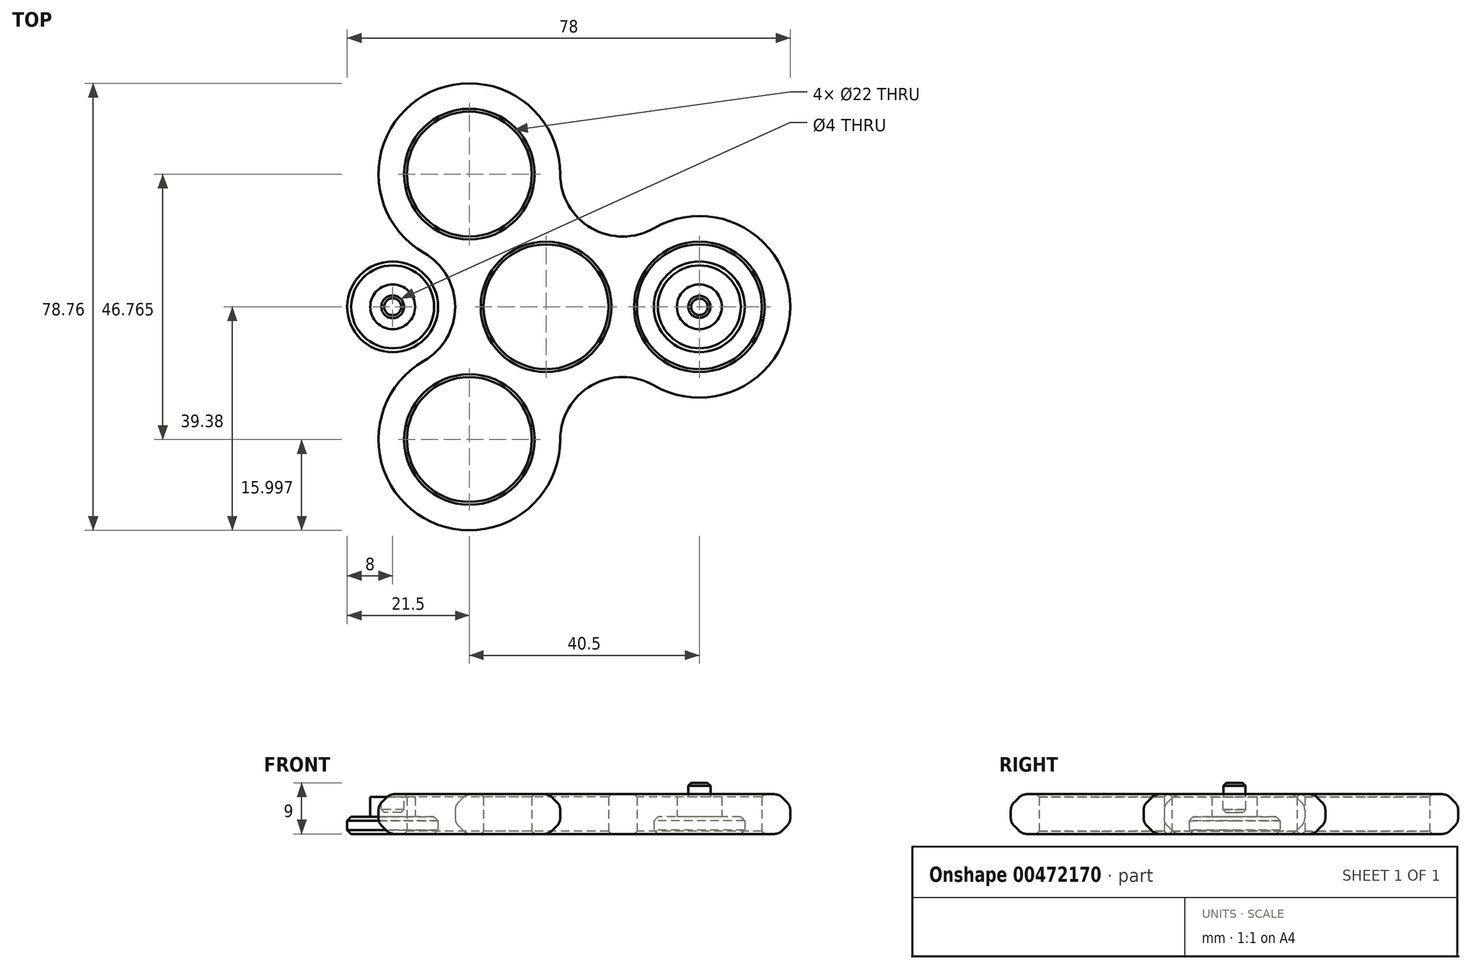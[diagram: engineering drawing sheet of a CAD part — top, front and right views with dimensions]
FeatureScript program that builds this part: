
annotation { "Feature Type Name" : "Feature", "Feature Type Description" : "" }
export const myFeature = defineFeature(function(context is Context, id is Id, definition is map)
    precondition{}
    {
        {
            var Q0;
            Q0=qCreatedBy(makeId("Top.planeOp"),FACE);
            var sketch = newSketch(context, id + "F0", { "sketchPlane" : qUnion([Q0])});
            skCircle(sketch, "E0", {"center": v(0, 0) * mm, "radius": 11 * mm});
            skCircle(sketch, "E1", {"center": v(27, 0) * mm, "radius": 11 * mm});
            skArc(sketch, "E2", {"start": v(19, -13.86) * mm, "mid": v(43, 0) * mm, "end": v(19, 13.86) * mm});
            skArc(sketch, "E3.1.0", {"start": v(2.5, 23.38) * mm, "mid": v(-21.5, 37.24) * mm, "end": v(-21.5, 9.53) * mm});
            skCircle(sketch, "E3.1.1", {"center": v(-13.5, 23.38) * mm, "radius": 11 * mm});
            skArc(sketch, "E3.2.0", {"start": v(-21.5, -9.53) * mm, "mid": v(-21.5, -37.24) * mm, "end": v(2.5, -23.38) * mm});
            skCircle(sketch, "E3.2.1", {"center": v(-13.5, -23.38) * mm, "radius": 11 * mm});
            skCircle(sketch, "E4", {"center": v(0, 0) * mm, "radius": 27 * mm, "construction": true});
            skArc(sketch, "E5", {"start": v(19, -13.86) * mm, "mid": v(8, -13.86) * mm, "end": v(2.5, -23.38) * mm});
            skArc(sketch, "E6.1.0", {"start": v(2.5, 23.38) * mm, "mid": v(8, 13.86) * mm, "end": v(19, 13.86) * mm});
            skArc(sketch, "E6.2.0", {"start": v(-21.5, -9.53) * mm, "mid": v(-16, 0) * mm, "end": v(-21.5, 9.53) * mm});
            skSolve(sketch);
        }
        {
            var Q0;
            Q0=makeQuery(id+"F0.imprint","IMPRINT",FACE,{"disambiguationData":[TD([[makeQuery(id+"F0.imprint","IMPRINT",EDGE,{"derivedFrom":sQuery(id+"F0.wireOp",EDGE,"E0")}),-1.0]])]});
            extrude(context, id + "F1", {"entities" : qUnion([Q0]), "depth" : 7 * mm});
        }
        {
            var Q0;
            Q0=makeQuery(id+"F1.opExtrude","CAP_EDGE",EDGE,{"disambiguationData":[OSD([sQuery(id+"F0.wireOp",EDGE,"E3.1.0")])],"isStart":false});
            var Q1;
            Q1=makeQuery(id+"F1.opExtrude","CAP_EDGE",EDGE,{"disambiguationData":[OSD([sQuery(id+"F0.wireOp",EDGE,"E3.1.0")])],"isStart":true});
            chamfer(context, id + "F2", {"entities" : qUnion([Q0, Q1]), "width" : 2 * mm, "tangentPropagation" : true});
        }
        {
            var Q0;
            Q0=makeQuery(id+"F1.opExtrude","CAP_EDGE",EDGE,{"disambiguationData":[OSD([sQuery(id+"F0.wireOp",EDGE,"UbmVktEc-A1EJ-kPAt-I6l8-VilQYZhR0Qmw")])],"isStart":false});
            var Q1;
            Q1=makeQuery(id+"F1.opExtrude","CAP_EDGE",EDGE,{"disambiguationData":[OSD([sQuery(id+"F0.wireOp",EDGE,"UbmVktEc-A1EJ-kPAt-I6l8-VilQYZhR0Qmw")])],"isStart":true});
            var Q2;
            Q2=makeQuery(id+"F1.opExtrude","CAP_EDGE",EDGE,{"disambiguationData":[OSD([sQuery(id+"F0.wireOp",EDGE,"E0")])],"isStart":false});
            var Q3;
            Q3=makeQuery(id+"F1.opExtrude","CAP_EDGE",EDGE,{"disambiguationData":[OSD([sQuery(id+"F0.wireOp",EDGE,"E0")])],"isStart":true});
            var Q4;
            Q4=makeQuery(id+"F1.opExtrude","CAP_EDGE",EDGE,{"disambiguationData":[OSD([sQuery(id+"F0.wireOp",EDGE,"E1")])],"isStart":false});
            var Q5;
            Q5=makeQuery(id+"F1.opExtrude","CAP_EDGE",EDGE,{"disambiguationData":[OSD([sQuery(id+"F0.wireOp",EDGE,"E1")])],"isStart":true});
            var Q6;
            Q6=makeQuery(id+"F1.opExtrude","CAP_EDGE",EDGE,{"disambiguationData":[OSD([sQuery(id+"F0.wireOp",EDGE,"E3.1.1")])],"isStart":false});
            var Q7;
            Q7=makeQuery(id+"F1.opExtrude","CAP_EDGE",EDGE,{"disambiguationData":[OSD([sQuery(id+"F0.wireOp",EDGE,"E3.1.1")])],"isStart":true});
            var Q8;
            Q8=makeQuery(id+"F1.opExtrude","CAP_EDGE",EDGE,{"disambiguationData":[OSD([sQuery(id+"F0.wireOp",EDGE,"E3.2.1")])],"isStart":true});
            var Q9;
            Q9=makeQuery(id+"F1.opExtrude","CAP_EDGE",EDGE,{"disambiguationData":[OSD([sQuery(id+"F0.wireOp",EDGE,"E3.2.1")])],"isStart":false});
            chamfer(context, id + "F3", {"entities" : qUnion([Q0, Q1, Q2, Q3, Q4, Q5, Q6, Q7, Q8, Q9]), "width" : 0.5 * mm, "tangentPropagation" : true});
        }
        {
            var Q0;
            {var subQ0=sQuery(id+"F0.wireOp",EDGE,"E3.1.0");Q0=makeQuery(id+"F2.opChamfer","BLEND_EDGE",EDGE,{"blendedFrom":[makeQuery(id+"F1.opExtrude","CAP_EDGE",EDGE,{"disambiguationData":[OSD([subQ0])],"isStart":false}),makeQuery(id+"F1.opExtrude","CAP_FACE",FACE,{"disambiguationData":[OSD([sQuery(id+"F0.wireOp",EDGE,"E0"),sQuery(id+"F0.wireOp",EDGE,"E1"),sQuery(id+"F0.wireOp",EDGE,"E2"),subQ0,sQuery(id+"F0.wireOp",EDGE,"E3.1.1"),sQuery(id+"F0.wireOp",EDGE,"E3.2.0"),sQuery(id+"F0.wireOp",EDGE,"E3.2.1"),sQuery(id+"F0.wireOp",EDGE,"E5"),sQuery(id+"F0.wireOp",EDGE,"E6.1.0"),sQuery(id+"F0.wireOp",EDGE,"E6.2.0")])],"isStart":false})],"blendedInto":[makeQuery(id+"F1.opExtrude","CAP_FACE",FACE,{"disambiguationData":[OSD([sQuery(id+"F0.wireOp",EDGE,"E0"),sQuery(id+"F0.wireOp",EDGE,"E1"),sQuery(id+"F0.wireOp",EDGE,"E2"),subQ0,sQuery(id+"F0.wireOp",EDGE,"E3.1.1"),sQuery(id+"F0.wireOp",EDGE,"E3.2.0"),sQuery(id+"F0.wireOp",EDGE,"E3.2.1"),sQuery(id+"F0.wireOp",EDGE,"E5"),sQuery(id+"F0.wireOp",EDGE,"E6.1.0"),sQuery(id+"F0.wireOp",EDGE,"E6.2.0")])],"isStart":false})]});}
            var Q1;
            {var subQ0=sQuery(id+"F0.wireOp",EDGE,"E3.1.0");Q1=makeQuery(id+"F2.opChamfer","BLEND_EDGE",EDGE,{"blendedFrom":[makeQuery(id+"F1.opExtrude","CAP_EDGE",EDGE,{"disambiguationData":[OSD([subQ0])],"isStart":false}),makeQuery(id+"F1.opExtrude","SWEPT_FACE",FACE,{"disambiguationData":[OSD([subQ0])]})],"blendedInto":[makeQuery(id+"F1.opExtrude","SWEPT_FACE",FACE,{"disambiguationData":[OSD([subQ0])]})]});}
            var Q2;
            {var subQ0=sQuery(id+"F0.wireOp",EDGE,"E3.1.0");Q2=makeQuery(id+"F2.opChamfer","BLEND_EDGE",EDGE,{"blendedFrom":[makeQuery(id+"F1.opExtrude","CAP_EDGE",EDGE,{"disambiguationData":[OSD([subQ0])],"isStart":true}),makeQuery(id+"F1.opExtrude","SWEPT_FACE",FACE,{"disambiguationData":[OSD([subQ0])]})],"blendedInto":[makeQuery(id+"F1.opExtrude","SWEPT_FACE",FACE,{"disambiguationData":[OSD([subQ0])]})]});}
            var Q3;
            {var subQ0=sQuery(id+"F0.wireOp",EDGE,"E3.1.0");Q3=makeQuery(id+"F2.opChamfer","BLEND_EDGE",EDGE,{"blendedFrom":[makeQuery(id+"F1.opExtrude","CAP_EDGE",EDGE,{"disambiguationData":[OSD([subQ0])],"isStart":true}),makeQuery(id+"F1.opExtrude","CAP_FACE",FACE,{"disambiguationData":[OSD([sQuery(id+"F0.wireOp",EDGE,"E0"),sQuery(id+"F0.wireOp",EDGE,"E1"),sQuery(id+"F0.wireOp",EDGE,"E2"),subQ0,sQuery(id+"F0.wireOp",EDGE,"E3.1.1"),sQuery(id+"F0.wireOp",EDGE,"E3.2.0"),sQuery(id+"F0.wireOp",EDGE,"E3.2.1"),sQuery(id+"F0.wireOp",EDGE,"E5"),sQuery(id+"F0.wireOp",EDGE,"E6.1.0"),sQuery(id+"F0.wireOp",EDGE,"E6.2.0")])],"isStart":true})],"blendedInto":[makeQuery(id+"F1.opExtrude","CAP_FACE",FACE,{"disambiguationData":[OSD([sQuery(id+"F0.wireOp",EDGE,"E0"),sQuery(id+"F0.wireOp",EDGE,"E1"),sQuery(id+"F0.wireOp",EDGE,"E2"),subQ0,sQuery(id+"F0.wireOp",EDGE,"E3.1.1"),sQuery(id+"F0.wireOp",EDGE,"E3.2.0"),sQuery(id+"F0.wireOp",EDGE,"E3.2.1"),sQuery(id+"F0.wireOp",EDGE,"E5"),sQuery(id+"F0.wireOp",EDGE,"E6.1.0"),sQuery(id+"F0.wireOp",EDGE,"E6.2.0")])],"isStart":true})]});}
            fillet(context, id + "F4", {"entities" : qUnion([Q0, Q1, Q2, Q3]), "radius" : 2 * mm, "tangentPropagation" : true, "allowEdgeOverflow" : false});
        }
        {
            var Q0;
            Q0=qCreatedBy(makeId("Top.planeOp"),FACE);
            var sketch = newSketch(context, id + "F5", { "sketchPlane" : qUnion([Q0])});
            skCircle(sketch, "E7", {"center": v(-27, 0) * mm, "radius": 8 * mm});
            skCircle(sketch, "E8", {"center": v(27, 0) * mm, "radius": 8 * mm});
            skSolve(sketch);
        }
        {
            var Q0;
            Q0=makeQuery(id+"F5.imprint","IMPRINT",FACE,{"disambiguationData":[TD([[makeQuery(id+"F5.imprint","IMPRINT",EDGE,{"derivedFrom":sQuery(id+"F5.wireOp",EDGE,"E7")}),1.0]])]});
            var Q1;
            Q1=makeQuery(id+"F5.imprint","IMPRINT",FACE,{"disambiguationData":[TD([[makeQuery(id+"F5.imprint","IMPRINT",EDGE,{"derivedFrom":sQuery(id+"F5.wireOp",EDGE,"E8")}),1.0]])]});
            extrude(context, id + "F6", {"entities" : qUnion([Q0, Q1]), "depth" : 3 * mm});
        }
        {
            var Q0;
            Q0=makeQuery(id+"F6.opExtrude","CAP_EDGE",EDGE,{"disambiguationData":[OSD([sQuery(id+"F5.wireOp",EDGE,"E7")])],"isStart":true});
            var Q1;
            Q1=makeQuery(id+"F6.opExtrude","CAP_EDGE",EDGE,{"disambiguationData":[OSD([sQuery(id+"F5.wireOp",EDGE,"E8")])],"isStart":true});
            var Q2;
            Q2=makeQuery(id+"F6.opExtrude","CAP_EDGE",EDGE,{"disambiguationData":[OSD([sQuery(id+"F5.wireOp",EDGE,"E7")])],"isStart":false});
            var Q3;
            Q3=makeQuery(id+"F6.opExtrude","CAP_EDGE",EDGE,{"disambiguationData":[OSD([sQuery(id+"F5.wireOp",EDGE,"E8")])],"isStart":false});
            chamfer(context, id + "F7", {"entities" : qUnion([Q0, Q1, Q2, Q3]), "width" : 0.7 * mm, "tangentPropagation" : true});
        }
        {
            var Q0;
            Q0=makeQuery(id+"F6.opExtrude","CAP_FACE",FACE,{"disambiguationData":[OSD([sQuery(id+"F5.wireOp",EDGE,"E8")])],"isStart":false});
            var sketch = newSketch(context, id + "F8", { "sketchPlane" : qUnion([Q0])});
            skCircle(sketch, "E9", {"center": v(27, 0) * mm, "radius": 3.95 * mm});
            skSolve(sketch);
        }
        {
            var Q0;
            Q0=qSketchRegion(id+"F8",true);
            extrude(context, id + "F9", {"entities" : qUnion([Q0]), "operationType" : NewBodyOperationType.ADD, "depth" : 3.5 * mm});
        }
        {
            var Q0;
            Q0=makeQuery(id+"F6.opExtrude","CAP_FACE",FACE,{"disambiguationData":[OSD([sQuery(id+"F5.wireOp",EDGE,"E7")])],"isStart":false});
            var sketch = newSketch(context, id + "F10", { "sketchPlane" : qUnion([Q0])});
            skCircle(sketch, "E10", {"center": v(-27, 0) * mm, "radius": 3.95 * mm});
            skSolve(sketch);
        }
        {
            var Q0;
            Q0=qSketchRegion(id+"F10",true);
            extrude(context, id + "F11", {"entities" : qUnion([Q0]), "operationType" : NewBodyOperationType.ADD, "depth" : 3.5 * mm});
        }
        {
            var Q0;
            Q0=makeQuery(id+"F9.opExtrude","CAP_FACE",FACE,{"disambiguationData":[OSD([sQuery(id+"F8.wireOp",EDGE,"E9")])],"isStart":false});
            var sketch = newSketch(context, id + "F12", { "sketchPlane" : qUnion([Q0])});
            skCircle(sketch, "E11", {"center": v(27, 0) * mm, "radius": 1.95 * mm});
            skSolve(sketch);
        }
        {
            var Q0;
            Q0=makeQuery(id+"F11.opExtrude","CAP_FACE",FACE,{"disambiguationData":[OSD([sQuery(id+"F10.wireOp",EDGE,"E10")])],"isStart":false});
            var sketch = newSketch(context, id + "F13", { "sketchPlane" : qUnion([Q0])});
            skCircle(sketch, "E12", {"center": v(-27, 0) * mm, "radius": 2 * mm});
            skSolve(sketch);
        }
        {
            var Q0;
            Q0=makeQuery(id+"F13.imprint","IMPRINT",FACE,{"disambiguationData":[TD([[makeQuery(id+"F13.imprint","IMPRINT",EDGE,{"derivedFrom":sQuery(id+"F13.wireOp",EDGE,"E12")}),1.0]])]});
            extrude(context, id + "F14", {"entities" : qUnion([Q0]), "operationType" : NewBodyOperationType.REMOVE, "oppositeDirection" : true, "depth" : 2.7 * mm});
        }
        {
            var Q0;
            Q0=makeQuery(id+"F12.imprint","IMPRINT",FACE,{"disambiguationData":[TD([[makeQuery(id+"F12.imprint","IMPRINT",EDGE,{"derivedFrom":sQuery(id+"F12.wireOp",EDGE,"E11")}),1.0]])]});
            extrude(context, id + "F15", {"entities" : qUnion([Q0]), "operationType" : NewBodyOperationType.ADD, "depth" : 2.5 * mm});
        }
        {
            var Q0;
            Q0=makeQuery(id+"F15.opExtrude","CAP_EDGE",EDGE,{"disambiguationData":[OSD([sQuery(id+"F12.wireOp",EDGE,"E11")])],"isStart":false});
            var Q1;
            Q1=makeQuery(id+"F15.opExtrude","CAP_EDGE",EDGE,{"disambiguationData":[OSD([sQuery(id+"F12.wireOp",EDGE,"E11")])],"isStart":true});
            var Q2;
            Q2=makeQuery(id+"F14.boolean.opBoolean","COPY",EDGE,{"derivedFrom":makeQuery(id+"F14.opExtrude","CAP_EDGE",EDGE,{"disambiguationData":[OSD([sQuery(id+"F13.wireOp",EDGE,"E12")])],"isStart":true})});
            var Q3;
            Q3=makeQuery(id+"F14.boolean.opBoolean","COPY",EDGE,{"derivedFrom":makeQuery(id+"F14.opExtrude","CAP_EDGE",EDGE,{"disambiguationData":[OSD([sQuery(id+"F13.wireOp",EDGE,"E12")])],"isStart":false})});
            var Q4;
            Q4=makeQuery(id+"F11.opExtrude","CAP_EDGE",EDGE,{"disambiguationData":[OSD([sQuery(id+"F10.wireOp",EDGE,"E10")])],"isStart":true});
            var Q5;
            Q5=makeQuery(id+"F9.opExtrude","CAP_EDGE",EDGE,{"disambiguationData":[OSD([sQuery(id+"F8.wireOp",EDGE,"E9")])],"isStart":true});
            chamfer(context, id + "F16", {"entities" : qUnion([Q0, Q1, Q2, Q3, Q4, Q5]), "width" : 0.5 * mm, "tangentPropagation" : true});
        }
    });
